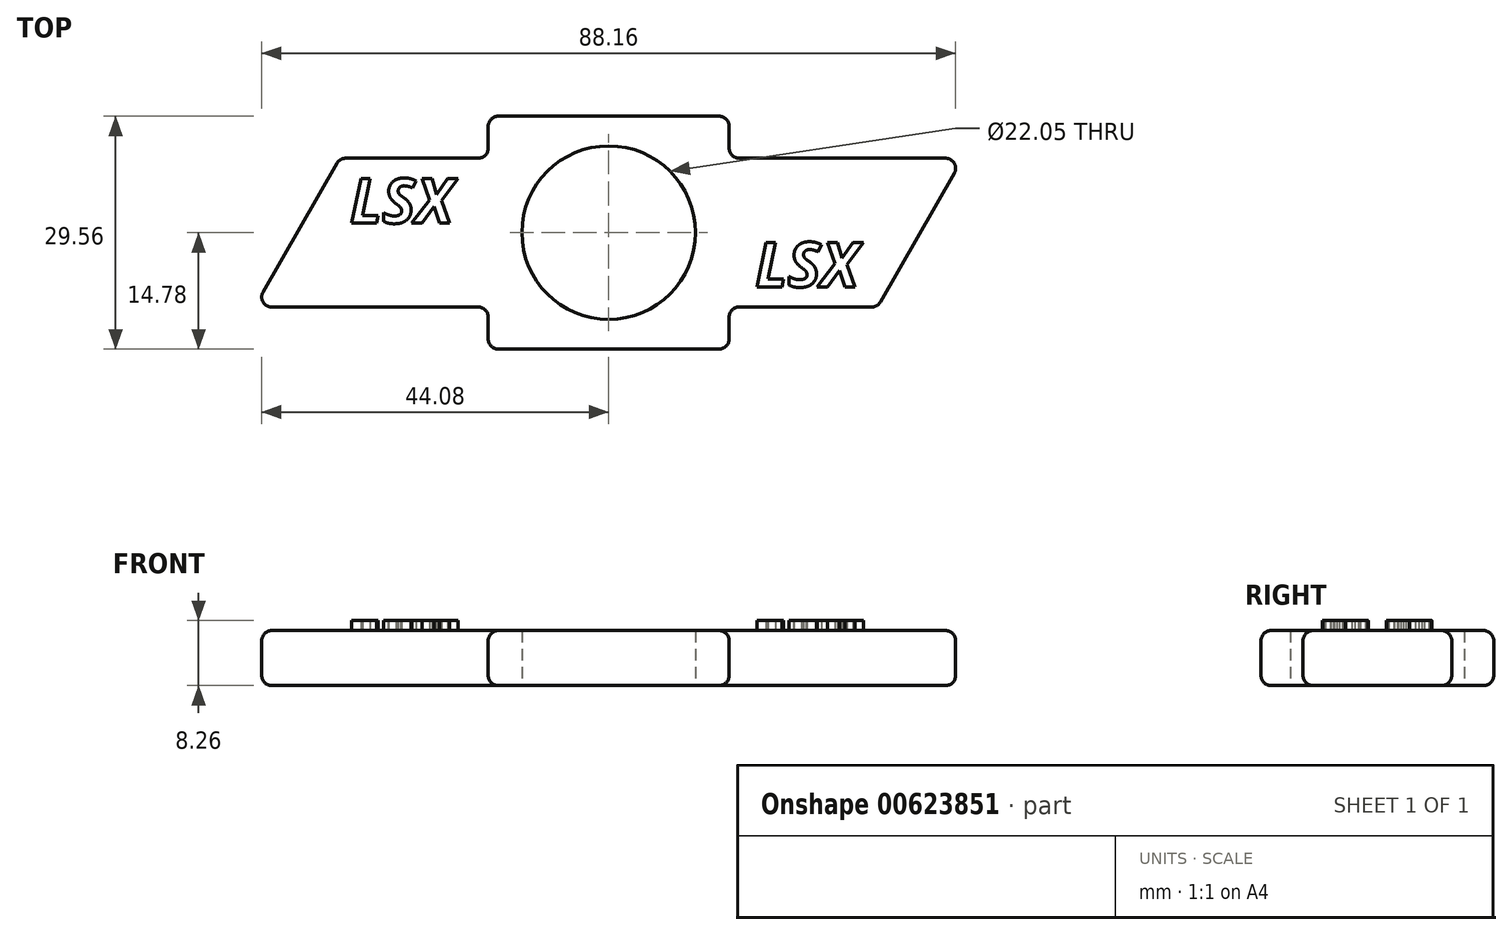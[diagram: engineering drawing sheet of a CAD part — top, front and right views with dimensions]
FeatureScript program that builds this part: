
annotation { "Feature Type Name" : "Feature", "Feature Type Description" : "" }
export const myFeature = defineFeature(function(context is Context, id is Id, definition is map)
    precondition{}
    {
        {
            var Q0;
            Q0=qCreatedBy(makeId("Top.planeOp"),FACE);
            var sketch = newSketch(context, id + "F0", { "sketchPlane" : qUnion([Q0])});
            skLineSegment(sketch, "E0", {"start": v(-38.42, -5.64) * mm, "end": v(-11.5, -5.64) * mm});
            skLineSegment(sketch, "E1", {"start": v(-38.42, -5.64) * mm, "end": v(-31.94, 5.64) * mm});
            skLineSegment(sketch, "E2", {"start": v(-31.94, 5.64) * mm, "end": v(-11.5, 5.64) * mm});
            skLineSegment(sketch, "E3", {"start": v(-11.5, 5.64) * mm, "end": v(-11.5, 10.97) * mm});
            skLineSegment(sketch, "E4", {"start": v(-11.5, -5.64) * mm, "end": v(-11.5, -10.97) * mm});
            skLineSegment(sketch, "E5", {"start": v(-11.5, 10.97) * mm, "end": v(11.5, 10.97) * mm});
            skLineSegment(sketch, "E6", {"start": v(-11.5, -10.97) * mm, "end": v(11.5, -10.97) * mm});
            skLineSegment(sketch, "E7", {"start": v(11.5, 10.97) * mm, "end": v(11.5, 5.64) * mm});
            skLineSegment(sketch, "E8", {"start": v(11.5, -10.97) * mm, "end": v(11.5, -5.64) * mm});
            skLineSegment(sketch, "E9", {"start": v(11.5, 5.64) * mm, "end": v(38.42, 5.64) * mm});
            skLineSegment(sketch, "E10", {"start": v(11.5, -5.64) * mm, "end": v(31.94, -5.64) * mm});
            skLineSegment(sketch, "E11", {"start": v(31.94, -5.64) * mm, "end": v(38.42, 5.64) * mm});
            skLineSegment(sketch, "E12", {"start": v(-11.5, 5.64) * mm, "end": v(-0.01, 5.64) * mm});
            skLineSegment(sketch, "E13", {"start": v(0, 10.97) * mm, "end": v(0, 0) * mm});
            skCircle(sketch, "E14", {"center": v(0, 0) * mm, "radius": 11.02 * mm});
            skLineSegment(sketch, "E15.0", {"start": v(-45, -9.45) * mm, "end": v(-34.15, 9.45) * mm});
            skLineSegment(sketch, "E15.1", {"start": v(15.3, 9.45) * mm, "end": v(45, 9.45) * mm});
            skLineSegment(sketch, "E15.2", {"start": v(15.3, 14.78) * mm, "end": v(15.3, 9.45) * mm});
            skLineSegment(sketch, "E15.3", {"start": v(-15.3, 14.78) * mm, "end": v(15.3, 14.78) * mm});
            skLineSegment(sketch, "E15.4", {"start": v(-15.3, 9.45) * mm, "end": v(-15.3, 14.78) * mm});
            skLineSegment(sketch, "E15.5", {"start": v(34.15, -9.45) * mm, "end": v(45, 9.45) * mm});
            skLineSegment(sketch, "E15.6", {"start": v(-34.15, 9.45) * mm, "end": v(-15.3, 9.45) * mm});
            skLineSegment(sketch, "E15.7", {"start": v(15.3, -9.45) * mm, "end": v(34.15, -9.45) * mm});
            skLineSegment(sketch, "E15.8", {"start": v(15.3, -14.78) * mm, "end": v(15.3, -9.45) * mm});
            skLineSegment(sketch, "E15.9", {"start": v(-15.3, -14.78) * mm, "end": v(15.3, -14.78) * mm});
            skLineSegment(sketch, "E15.10", {"start": v(-15.3, -9.45) * mm, "end": v(-15.3, -14.78) * mm});
            skLineSegment(sketch, "E15.11", {"start": v(-45, -9.45) * mm, "end": v(-15.3, -9.45) * mm});
            skSolve(sketch);
        }
        {
            var Q0;
            Q0 = qSketchRegion(id + "F0", true);
            var Q1;
            Q1=makeQuery(id+"F0.imprint","IMPRINT",FACE,{"disambiguationData":[TD([[makeQuery(id+"F0.imprint","IMPRINT",EDGE,{"derivedFrom":sQuery(id+"F0.wireOp",EDGE,"E0")}),1.0]])]});
            var Q2;
            {var subQ0=sQuery(id+"F0.wireOp",EDGE,"E3");Q2=makeQuery(id+"F0.imprint","IMPRINT",FACE,{"disambiguationData":[TD([[makeQuery(id+"F0.imprint","IMPRINT",EDGE,{"derivedFrom":subQ0}),-1.0]])]});}
            var Q3;
            {var subQ0=sQuery(id+"F0.wireOp",EDGE,"E7");Q3=makeQuery(id+"F0.imprint","IMPRINT",FACE,{"disambiguationData":[TD([[makeQuery(id+"F0.imprint","IMPRINT",EDGE,{"derivedFrom":subQ0}),-1.0]])]});}
            extrude(context, id + "F1", {"entities" : qUnion([Q0, Q1, Q2, Q3]), "depth" : 7 * mm, "offsetDistance" : 25.4 * mm});
        }
        {
            var Q0;
            Q0=makeQuery(id+"F1.opExtrude","CAP_FACE",FACE,{"disambiguationData":[OSD([sQuery(id+"F0.wireOp",EDGE,"E14"),sQuery(id+"F0.wireOp",EDGE,"E15.0"),sQuery(id+"F0.wireOp",EDGE,"E15.1"),sQuery(id+"F0.wireOp",EDGE,"E15.2"),sQuery(id+"F0.wireOp",EDGE,"E15.3"),sQuery(id+"F0.wireOp",EDGE,"E15.4"),sQuery(id+"F0.wireOp",EDGE,"E15.5"),sQuery(id+"F0.wireOp",EDGE,"E15.6"),sQuery(id+"F0.wireOp",EDGE,"E15.7"),sQuery(id+"F0.wireOp",EDGE,"E15.8"),sQuery(id+"F0.wireOp",EDGE,"E15.9"),sQuery(id+"F0.wireOp",EDGE,"E15.10"),sQuery(id+"F0.wireOp",EDGE,"E15.11")])],"isStart":false});
            var sketch = newSketch(context, id + "F2", { "sketchPlane" : qUnion([Q0])});
            skText(sketch, "E16", { "text": "LSX", "fontName": "OpenSans-BoldItalic.ttf"});
            skText(sketch, "E17", { "text": "LSX", "fontName": "OpenSans-BoldItalic.ttf"});
            const initialGuessF2  = {"E16": [-0.03288, 0.0012, 1, 0, 0.00572], "E17": [0.01861, -0.0069, 1, 0, 0.00572]};
            skSetInitialGuess(sketch, initialGuessF2);
            skSolve(sketch);
        }
        {
            var Q0;
            Q0 = qSketchRegion(id + "F2", true);
            extrude(context, id + "F3", {"entities" : qUnion([Q0]), "operationType" : NewBodyOperationType.ADD, "depth" : 1.27 * mm, "offsetDistance" : 25.4 * mm});
        }
        {
            var Q0;
            Q0=makeQuery(id+"F1.opExtrude","SWEPT_EDGE",EDGE,{"disambiguationData":[OSD([sQuery(id+"F0.wireOp",EDGE,"E15.0"),sQuery(id+"F0.wireOp",EDGE,"E15.6")])]});
            var Q1;
            Q1=makeQuery(id+"F1.opExtrude","SWEPT_EDGE",EDGE,{"disambiguationData":[OSD([sQuery(id+"F0.wireOp",EDGE,"E15.3"),sQuery(id+"F0.wireOp",EDGE,"E15.4")])]});
            var Q2;
            Q2=makeQuery(id+"F1.opExtrude","SWEPT_EDGE",EDGE,{"disambiguationData":[OSD([sQuery(id+"F0.wireOp",EDGE,"E15.2"),sQuery(id+"F0.wireOp",EDGE,"E15.3")])]});
            var Q3;
            Q3=makeQuery(id+"F1.opExtrude","SWEPT_EDGE",EDGE,{"disambiguationData":[OSD([sQuery(id+"F0.wireOp",EDGE,"E15.1"),sQuery(id+"F0.wireOp",EDGE,"E15.2")])]});
            var Q4;
            Q4=makeQuery(id+"F1.opExtrude","SWEPT_EDGE",EDGE,{"disambiguationData":[OSD([sQuery(id+"F0.wireOp",EDGE,"E15.1"),sQuery(id+"F0.wireOp",EDGE,"E15.5")])]});
            var Q5;
            Q5=makeQuery(id+"F1.opExtrude","SWEPT_EDGE",EDGE,{"disambiguationData":[OSD([sQuery(id+"F0.wireOp",EDGE,"E15.8"),sQuery(id+"F0.wireOp",EDGE,"E15.9")])]});
            var Q6;
            Q6=makeQuery(id+"F1.opExtrude","SWEPT_EDGE",EDGE,{"disambiguationData":[OSD([sQuery(id+"F0.wireOp",EDGE,"E15.7"),sQuery(id+"F0.wireOp",EDGE,"E15.8")])]});
            var Q7;
            Q7=makeQuery(id+"F1.opExtrude","SWEPT_EDGE",EDGE,{"disambiguationData":[OSD([sQuery(id+"F0.wireOp",EDGE,"E15.5"),sQuery(id+"F0.wireOp",EDGE,"E15.7")])]});
            var Q8;
            Q8=makeQuery(id+"F1.opExtrude","SWEPT_EDGE",EDGE,{"disambiguationData":[OSD([sQuery(id+"F0.wireOp",EDGE,"E15.9"),sQuery(id+"F0.wireOp",EDGE,"E15.10")])]});
            var Q9;
            Q9=makeQuery(id+"F1.opExtrude","SWEPT_EDGE",EDGE,{"disambiguationData":[OSD([sQuery(id+"F0.wireOp",EDGE,"E15.0"),sQuery(id+"F0.wireOp",EDGE,"E15.11")])]});
            var Q10;
            Q10=makeQuery(id+"F1.opExtrude","SWEPT_EDGE",EDGE,{"disambiguationData":[OSD([sQuery(id+"F0.wireOp",EDGE,"E15.10"),sQuery(id+"F0.wireOp",EDGE,"E15.11")])]});
            var Q11;
            Q11=makeQuery(id+"F1.opExtrude","SWEPT_EDGE",EDGE,{"disambiguationData":[OSD([sQuery(id+"F0.wireOp",EDGE,"E15.4"),sQuery(id+"F0.wireOp",EDGE,"E15.6")])]});
            fillet(context, id + "F4", {"entities" : qUnion([Q0, Q1, Q2, Q3, Q4, Q5, Q6, Q7, Q8, Q9, Q10, Q11]), "radius" : 1.27 * mm, "tangentPropagation" : true, "allowEdgeOverflow" : false});
        }
        {
            var Q0;
            Q0=makeQuery(id+"F1.opExtrude","CAP_EDGE",EDGE,{"disambiguationData":[OSD([sQuery(id+"F0.wireOp",EDGE,"E15.0")])],"isStart":false});
            fillet(context, id + "F5", {"entities" : qUnion([Q0]), "radius" : 1.27 * mm, "tangentPropagation" : true, "allowEdgeOverflow" : false});
        }
        {
            var Q0;
            Q0=makeQuery(id+"F1.opExtrude","CAP_EDGE",EDGE,{"disambiguationData":[OSD([sQuery(id+"F0.wireOp",EDGE,"E15.6")])],"isStart":true});
            fillet(context, id + "F6", {"entities" : qUnion([Q0]), "radius" : 1.27 * mm, "tangentPropagation" : true, "allowEdgeOverflow" : false});
        }
    });
